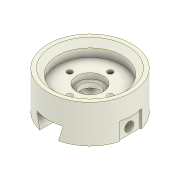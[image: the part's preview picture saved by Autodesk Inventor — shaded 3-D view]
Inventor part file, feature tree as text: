
AUTODESK INVENTOR PART (.ipt)
format: ipt  version: 2022 (Build 260153000, 153)  size: 420,864 bytes
history: native  units: mm
features: sketch x15, extrude x8, hole x6, projected_geometry x5, plane x3, mirror x2, chamfer x2, thicken_offset x1, fillet x1, split x1
ambient origin geometry x8: Origin, YZ Plane, XZ Plane, XY Plane, X Axis, Y Axis, Z Axis, Center Point
bodies: Solid1 (feature_tree), Solid2 (feature_tree), Solid3 (feature_tree)
feature tree (44):
  extrude  "Extrusion1"  Depth=5.0mm TaperAngle=0.0deg
  extrude  "Extrusion2"  Depth=40.0mm TaperAngle=0.0deg
  sketch  "Sketch4"  dims[d9=6.0mm d10=4.0mm d11=2.0mm d12=90.0deg d13=6.0mm d14=0.0mm d15=24.0mm]
  hole  "Hole1"  [1 undecoded]
  mirror  "Mirror1"
  hole  "Hole5"  [1 undecoded]
  thicken_offset  "Thicken1"
  extrude  "Extrusion3"  Depth=5.0mm
  extrude  "Extrusion4"  Depth=2.0mm TaperAngle=45.0deg
  fillet  "Fillet1"  Radius=0.15mm
  hole  "Hole2"  [1 undecoded]
  hole  "Hole3"  [1 undecoded]
  chamfer  "Chamfer1"  Distance=5.0mm
  chamfer  "Chamfer2"  Distance=6.5mm
  plane  "Work Plane1"
  split  "Split1"
  extrude  "Extrusion5"  Depth=9.0mm
  sketch  "Sketch12"  dims[d51=0.15mm]
  plane  "Work Plane2"
  extrude  "Extrusion8"  Depth=5.0mm
  plane  "Work Plane3"
  hole  "Hole9"  [1 undecoded]
  extrude  "Extrusion10"  Depth=15.5mm
  mirror  "Mirror2"
  extrude  "Extrusion11"  Depth=8.0mm
  hole  "Hole10"  [1 undecoded]
  sketch  "Sketch1"  dims[d1=5.0mm d2=24.25mm d3=0.0mm]
  sketch  "Sketch2"  dims[d5=3.0mm d6=40.0mm d7=0.0mm]
  sketch  "Sketch3"  dims[d8=13.0mm]
  sketch  "Sketch5"  dims[d16=5.0mm d17=0.0mm d18=0.0mm d19=0.0mm]
  sketch  "Sketch6"  dims[d20=5.0mm d21=15.0mm]
  sketch  "Sketch7"  dims[d22=40.0mm d24=360.0deg]
  sketch  "Sketch9"  dims[d26=2.0mm d27=6.0mm d28=4.0mm d29=2.0mm d30=90.0deg d31=5.0mm d32=20.594885mm]
  sketch  "Sketch10"  dims[d33=10.0mm d34=6.0mm d35=4.0mm d36=2.0mm d37=90.0deg d38=2.0mm d39=0.0mm d40=2.0mm d41=2.0mm d42=45.0deg d50=0.15mm]
  sketch  "Sketch18"  dims[d52=7.0mm d53=6.0mm d54=4.0mm d55=2.0mm d56=90.0deg d57=6.0mm d58=0.0mm d59=0.5mm d60=2.0mm d61=45.0deg]
  sketch  "Sketch19"  dims[d62=-7.0mm d63=7.0mm]
  sketch  "Sketch22"  dims[d64=7.0mm d65=5.0mm d66=0.0mm]
  sketch  "Sketch24"  dims[d67=14.75mm]
  sketch  "Sketch25"  dims[d68=-14.75mm d97=6.5mm d98=9.0mm d99=5.0mm d100=0.0mm d101=0.0mm d102=15.5mm d104=3.4mm d105=6.0mm d106=4.0mm d107=2.0mm d108=90.0deg d109=8.0mm d110=20.594885mm d117=8.0mm d118=8.0mm d119=1.0mm d120=0.0mm d121=0.2mm d122=0.0mm d123=0.0mm d124=7.0mm d125=6.0mm d126=4.0mm d127=2.0mm d128=90.0deg d129=8.0mm d130=20.594885mm d43=0.15mm d44=0.25mm d45=0.375mm d46=14.3117mm d47=0.75mm d48=20.594885mm d49=0.0625mm]
  projected_geometry  "Project Cut Edges1"
  projected_geometry  "Project Cut Edges2"
  projected_geometry  "Project Cut Edges3"
  projected_geometry  "Project Cut Edges4"
  projected_geometry  "Project Cut Edges5"
note: 6 required parameter values undecoded (feature->parameter linkage not recoverable at this tier; creation-order binding heuristic only, values carry confidence <= 0.55)
